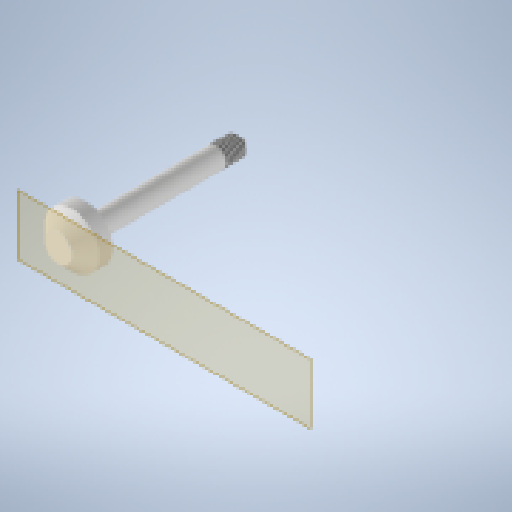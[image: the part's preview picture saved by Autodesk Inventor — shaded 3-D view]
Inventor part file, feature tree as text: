
AUTODESK INVENTOR PART (.ipt)
format: ipt  version: 2024 (Build 280153000, 153)  size: 166,912 bytes
history: native  units: mm
features: other x3, extrude x2, chamfer x2, sketch x2, reference x2, plane x1, thread x1
ambient origin geometry x8: Origin, YZ Plane, XZ Plane, XY Plane, X Axis, Y Axis, Z Axis, Center Point
bodies: Solid1 (feature_tree)
feature tree (13):
  plane  "Work Plane1"
  extrude  "Extrusion1"  Depth=27.0mm TaperAngle=0.0deg
  extrude  "Extrusion2"  Depth=1.0mm TaperAngle=45.0deg
  chamfer  "Chamfer1"  Distance=4.0mm
  thread  "Thread1"  [1 undecoded]
  chamfer  "Chamfer2"  [1 undecoded]
  sketch  "Sketch1"  dims[d0=3.0mm d1=27.0mm d2=0.0mm]
  reference  "Reference1"
  sketch  "Sketch2"  dims[d3=4.0mm d4=0.0mm d5=2.0mm d6=2.0mm d7=45.0deg d8=4.0mm d9=19.0mm d10=1.0mm d11=2.0mm d12=45.0deg]
  reference  "Reference2"
  other  "<userpath> windows\Documents\Inventor\Robotska_roka\roka_asemb.iam"
  other  "roka_asemb.iam"
  other  "povezava:2"
note: 2 required parameter values undecoded (feature->parameter linkage not recoverable at this tier; creation-order binding heuristic only, values carry confidence <= 0.55)
